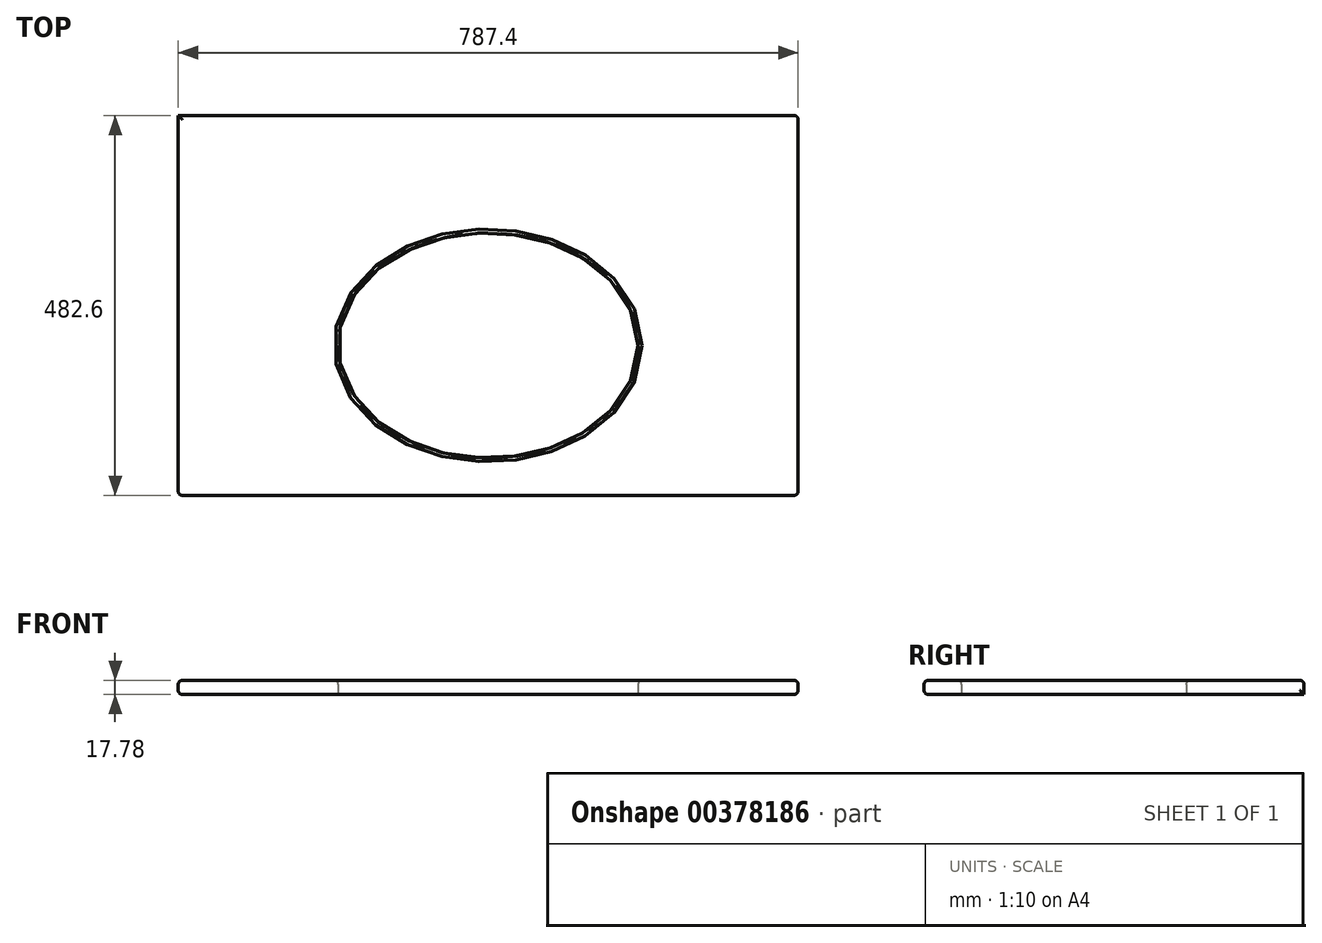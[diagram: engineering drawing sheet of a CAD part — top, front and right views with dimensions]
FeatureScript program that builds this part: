
annotation { "Feature Type Name" : "Feature", "Feature Type Description" : "" }
export const myFeature = defineFeature(function(context is Context, id is Id, definition is map)
    precondition{}
    {
        {
            var Q0;
            Q0=qCreatedBy(makeId("Top.planeOp"),FACE);
            var sketch = newSketch(context, id + "F0", { "sketchPlane" : qUnion([Q0])});
            skLineSegment(sketch, "E0.bottom", {"start": v(0, 0) * mm, "end": v(787.4, 0) * mm});
            skLineSegment(sketch, "E0.top", {"start": v(0, -482.6) * mm, "end": v(787.4, -482.6) * mm});
            skLineSegment(sketch, "E0.left", {"start": v(0, 0) * mm, "end": v(0, -482.6) * mm});
            skLineSegment(sketch, "E0.right", {"start": v(787.4, 0) * mm, "end": v(787.4, -482.6) * mm});
            skLineSegment(sketch, "E1", {"start": v(787.4, 0) * mm, "end": v(0, -482.6) * mm, "construction": true});
            skLineSegment(sketch, "E2", {"start": v(393.7, -241.3) * mm, "end": v(393.7, -292.1) * mm, "construction": true});
            skEllipse(sketch, "E3", {"center": v(393.7, -292.1) * mm, "majorRadius": 190.5 * mm, "minorRadius": 142.88 * mm, "majorAxis": v(1, 0)});
            skLineSegment(sketch, "E4", {"start": v(393.7, -482.6) * mm, "end": v(393.7, -434.98) * mm, "construction": true});
            skSolve(sketch);
        }
        {
            var Q0;
            Q0=makeQuery(id+"F0.imprint","IMPRINT",FACE,{"disambiguationData":[TD([[makeQuery(id+"F0.imprint","IMPRINT",EDGE,{"derivedFrom":sQuery(id+"F0.wireOp",EDGE,"E0.bottom")}),-1.0]])]});
            extrude(context, id + "F1", {"entities" : qUnion([Q0]), "depth" : 17.78 * mm});
        }
        {
            var Q0;
            Q0=makeQuery(id+"F1.opExtrude","SWEPT_FACE",FACE,{"disambiguationData":[OSD([sQuery(id+"F0.wireOp",EDGE,"E0.top")])]});
            var Q1;
            Q1=makeQuery(id+"F1.opExtrude","SWEPT_FACE",FACE,{"disambiguationData":[OSD([sQuery(id+"F0.wireOp",EDGE,"E0.right")])]});
            var Q2;
            Q2=makeQuery(id+"F1.opExtrude","CAP_FACE",FACE,{"disambiguationData":[OSD([sQuery(id+"F0.wireOp",EDGE,"E0.bottom"),sQuery(id+"F0.wireOp",EDGE,"E0.top"),sQuery(id+"F0.wireOp",EDGE,"E0.left"),sQuery(id+"F0.wireOp",EDGE,"E0.right"),sQuery(id+"F0.wireOp",EDGE,"E3")])],"isStart":false});
            var Q3;
            Q3=makeQuery(id+"F1.opExtrude","CAP_EDGE",EDGE,{"disambiguationData":[OSD([sQuery(id+"F0.wireOp",EDGE,"E0.left")])],"isStart":true});
            fillet(context, id + "F2", {"entities" : qUnion([Q0, Q1, Q2, Q3]), "radius" : 5.08 * mm, "tangentPropagation" : true, "allowEdgeOverflow" : false});
        }
    });
